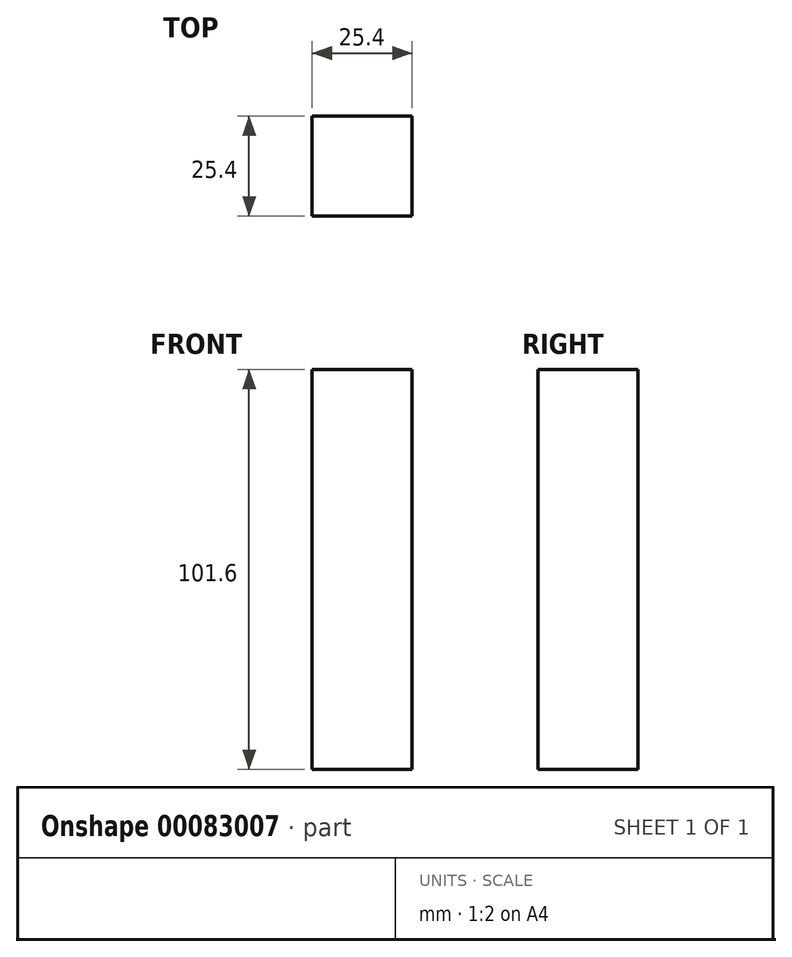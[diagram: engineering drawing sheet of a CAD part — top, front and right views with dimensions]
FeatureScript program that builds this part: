
annotation { "Feature Type Name" : "Feature", "Feature Type Description" : "" }
export const myFeature = defineFeature(function(context is Context, id is Id, definition is map)
    precondition{}
    {
        {
            var Q0;
            Q0=qCreatedBy(makeId("Top.planeOp"),FACE);
            var sketch = newSketch(context, id + "F0", { "sketchPlane" : qUnion([Q0])});
            skLineSegment(sketch, "E0.bottom", {"start": v(-144.78, 35.68) * mm, "end": v(-119.38, 35.68) * mm});
            skLineSegment(sketch, "E0.top", {"start": v(-144.78, 10.28) * mm, "end": v(-119.38, 10.28) * mm});
            skLineSegment(sketch, "E0.left", {"start": v(-144.78, 35.68) * mm, "end": v(-144.78, 10.28) * mm});
            skLineSegment(sketch, "E0.right", {"start": v(-119.38, 35.68) * mm, "end": v(-119.38, 10.28) * mm});
            skSolve(sketch);
        }
        {
            var Q0;
            Q0=makeQuery(id+"F0.imprint","IMPRINT",FACE,{"disambiguationData":[TD([[makeQuery(id+"F0.imprint","IMPRINT",EDGE,{"derivedFrom":sQuery(id+"F0.wireOp",EDGE,"E0.bottom")}),-1.0]])]});
            extrude(context, id + "F1", {"entities" : qUnion([Q0]), "depth" : 101.6 * mm});
        }
    });
